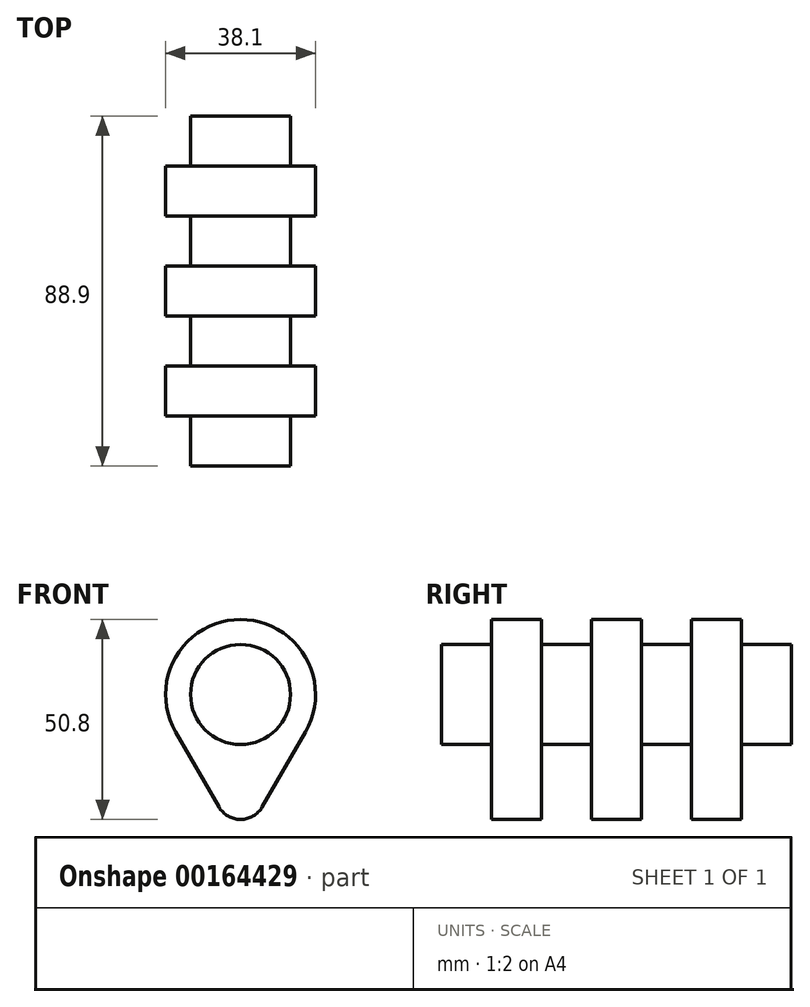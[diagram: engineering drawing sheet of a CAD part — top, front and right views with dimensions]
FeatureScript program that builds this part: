
annotation { "Feature Type Name" : "Feature", "Feature Type Description" : "" }
export const myFeature = defineFeature(function(context is Context, id is Id, definition is map)
    precondition{}
    {
        {
            var Q0;
            Q0=qCreatedBy(makeId("Front.planeOp"),FACE);
            var sketch = newSketch(context, id + "F0", { "sketchPlane" : qUnion([Q0])});
            skCircle(sketch, "E0", {"center": v(0, 0) * mm, "radius": 12.7 * mm});
            skSolve(sketch);
        }
        {
            var Q0;
            Q0=makeQuery(id+"F0.imprint","IMPRINT",FACE,{"disambiguationData":[TD([[makeQuery(id+"F0.imprint","IMPRINT",EDGE,{"derivedFrom":sQuery(id+"F0.wireOp",EDGE,"E0")}),1.0]])]});
            extrude(context, id + "F1", {"entities" : qUnion([Q0]), "depth" : 88.9 * mm});
        }
        {
            var Q0;
            Q0=qCreatedBy(makeId("Front.planeOp"),FACE);
            cPlane(context, id + "F2", {"entities" : qUnion([Q0]), "cplaneType" : CPlaneType.OFFSET, "offset" : 12.7 * mm, "width" : 152.4 * mm, "height" : 152.4 * mm});
        }
        {
            var Q0;
            Q0=qCreatedBy(id+"F2.planeOp",FACE);
            var sketch = newSketch(context, id + "F3", { "sketchPlane" : qUnion([Q0])});
            skCircle(sketch, "E1", {"center": v(0, 0) * mm, "radius": 12.7 * mm});
            skArc(sketch, "E2", {"start": v(16.5, -9.52) * mm, "mid": v(0, 19.05) * mm, "end": v(-16.5, -9.52) * mm});
            skArc(sketch, "E3", {"start": v(-5.5, -28.58) * mm, "mid": v(0, -31.75) * mm, "end": v(5.5, -28.58) * mm});
            skLineSegment(sketch, "E4", {"start": v(-5.5, -28.58) * mm, "end": v(-16.5, -9.52) * mm});
            skLineSegment(sketch, "E5", {"start": v(5.5, -28.58) * mm, "end": v(16.5, -9.52) * mm});
            skSolve(sketch);
        }
        {
            var Q0;
            Q0=makeQuery(id+"F3.imprint","IMPRINT",FACE,{"disambiguationData":[TD([[makeQuery(id+"F3.imprint","IMPRINT",EDGE,{"derivedFrom":sQuery(id+"F3.wireOp",EDGE,"E1")}),-1.0]])]});
            extrude(context, id + "F4", {"entities" : qUnion([Q0]), "operationType" : NewBodyOperationType.ADD, "depth" : 12.7 * mm});
        }
        {
            var Q0;
            Q0=qCreatedBy(id+"F2.planeOp",FACE);
            cPlane(context, id + "F5", {"entities" : qUnion([Q0]), "cplaneType" : CPlaneType.OFFSET, "offset" : 25.4 * mm, "width" : 152.4 * mm, "height" : 152.4 * mm});
        }
        {
            var Q0;
            Q0=qCreatedBy(id+"F5.planeOp",FACE);
            var sketch = newSketch(context, id + "F6", { "sketchPlane" : qUnion([Q0])});
            skCircle(sketch, "E6", {"center": v(0, 0) * mm, "radius": 12.7 * mm});
            skArc(sketch, "E7", {"start": v(16.5, -9.53) * mm, "mid": v(0, 19.05) * mm, "end": v(-16.5, -9.52) * mm});
            skArc(sketch, "E8", {"start": v(-5.5, -28.57) * mm, "mid": v(0, -31.75) * mm, "end": v(5.5, -28.58) * mm});
            skLineSegment(sketch, "E9", {"start": v(-5.5, -28.58) * mm, "end": v(-16.5, -9.52) * mm});
            skLineSegment(sketch, "E10", {"start": v(16.5, -9.53) * mm, "end": v(5.5, -28.58) * mm});
            skSolve(sketch);
        }
        {
            var Q0;
            Q0=makeQuery(id+"F6.imprint","IMPRINT",FACE,{"disambiguationData":[TD([[makeQuery(id+"F6.imprint","IMPRINT",EDGE,{"derivedFrom":sQuery(id+"F6.wireOp",EDGE,"E6")}),-1.0]])]});
            extrude(context, id + "F7", {"entities" : qUnion([Q0]), "operationType" : NewBodyOperationType.ADD, "depth" : 12.7 * mm});
        }
        {
            var Q0;
            Q0=qCreatedBy(id+"F5.planeOp",FACE);
            cPlane(context, id + "F8", {"entities" : qUnion([Q0]), "cplaneType" : CPlaneType.OFFSET, "offset" : 25.4 * mm, "width" : 152.4 * mm, "height" : 152.4 * mm});
        }
        {
            var Q0;
            Q0=qCreatedBy(id+"F8.planeOp",FACE);
            var sketch = newSketch(context, id + "F9", { "sketchPlane" : qUnion([Q0])});
            skArc(sketch, "E11", {"start": v(16.5, -9.53) * mm, "mid": v(0, 19.05) * mm, "end": v(-16.5, -9.52) * mm});
            skCircle(sketch, "E12", {"center": v(0, 0) * mm, "radius": 12.7 * mm});
            skArc(sketch, "E13", {"start": v(-5.5, -28.58) * mm, "mid": v(0, -31.75) * mm, "end": v(5.5, -28.58) * mm});
            skLineSegment(sketch, "E14", {"start": v(-16.5, -9.52) * mm, "end": v(-5.5, -28.58) * mm});
            skLineSegment(sketch, "E15", {"start": v(16.5, -9.53) * mm, "end": v(5.5, -28.58) * mm});
            skSolve(sketch);
        }
        {
            var Q0;
            Q0=makeQuery(id+"F9.imprint","IMPRINT",FACE,{"disambiguationData":[TD([[makeQuery(id+"F9.imprint","IMPRINT",EDGE,{"derivedFrom":sQuery(id+"F9.wireOp",EDGE,"E11")}),1.0]])]});
            extrude(context, id + "F10", {"entities" : qUnion([Q0]), "operationType" : NewBodyOperationType.ADD, "depth" : 12.7 * mm});
        }
    });
